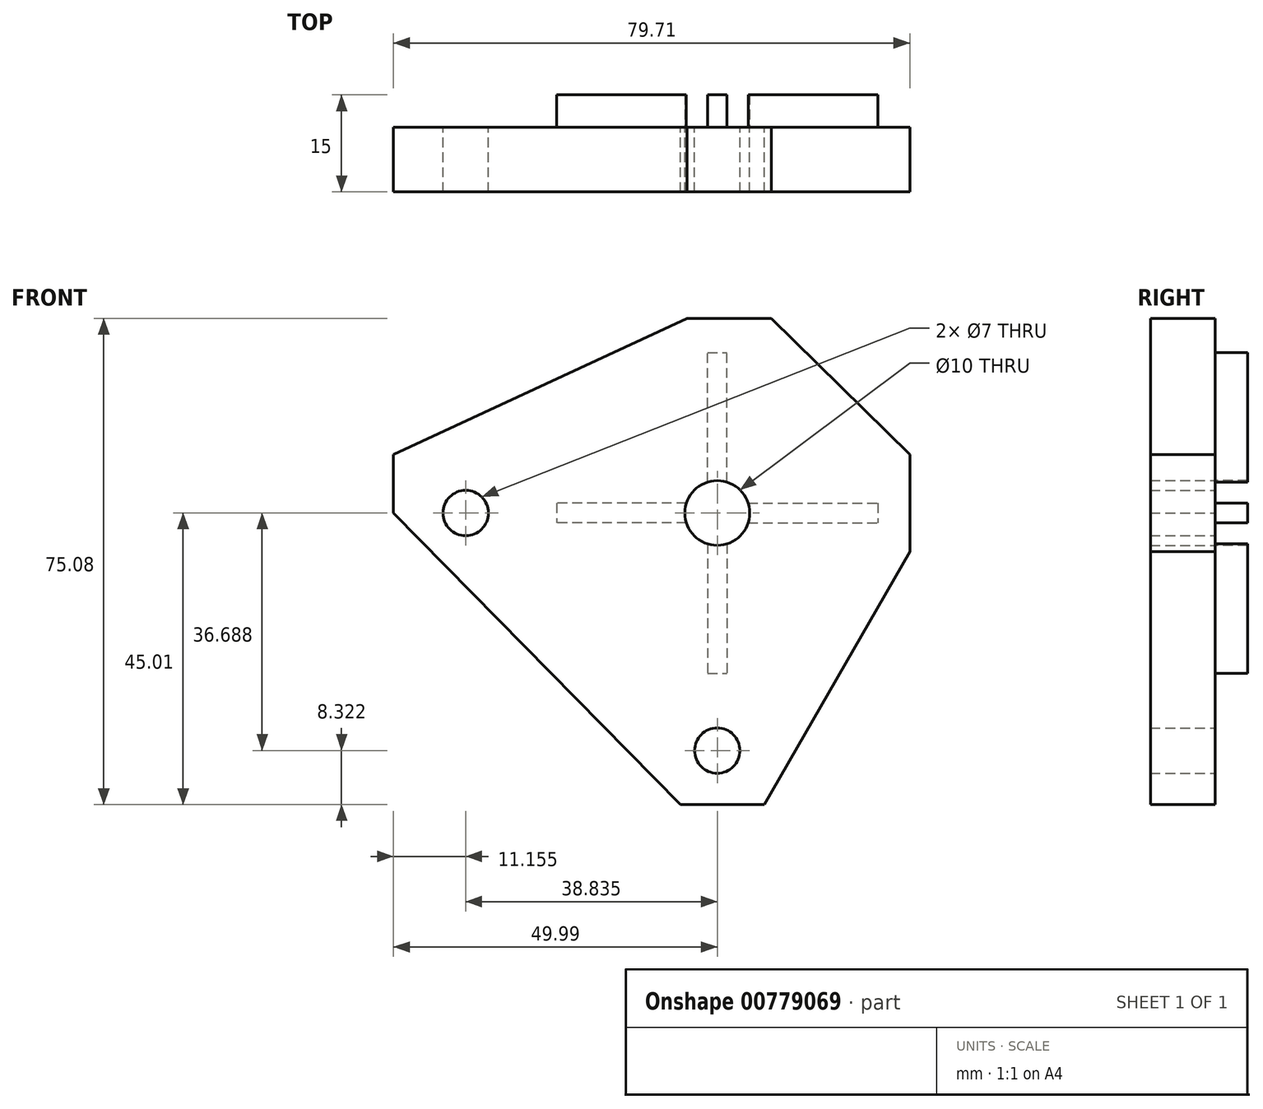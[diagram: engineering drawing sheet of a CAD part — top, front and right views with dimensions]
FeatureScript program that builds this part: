
annotation { "Feature Type Name" : "Feature", "Feature Type Description" : "" }
export const myFeature = defineFeature(function(context is Context, id is Id, definition is map)
    precondition{}
    {
        {
            var Q0;
            Q0=qCreatedBy(makeId("Front.planeOp"),FACE);
            var sketch = newSketch(context, id + "F0", { "sketchPlane" : qUnion([Q0])});
            skCircle(sketch, "E0", {"center": v(0, 0) * mm, "radius": 5 * mm});
            skLineSegment(sketch, "E1", {"start": v(0, 30.64) * mm, "end": v(0, -43.55) * mm, "construction": true});
            skLineSegment(sketch, "E2", {"start": v(-1.5, 4.77) * mm, "end": v(-1.5, 24.77) * mm});
            skLineSegment(sketch, "E3.MirrorCS", {"start": v(1.5, 4.77) * mm, "end": v(1.5, 24.77) * mm});
            skLineSegment(sketch, "E4", {"start": v(-1.5, 24.77) * mm, "end": v(1.5, 24.77) * mm});
            skLineSegment(sketch, "E5", {"start": v(-38.83, 0) * mm, "end": v(36.67, 0) * mm, "construction": true});
            skLineSegment(sketch, "E6.MirrorCS", {"start": v(1.5, -4.77) * mm, "end": v(1.5, -24.77) * mm});
            skLineSegment(sketch, "E7.MirrorCS", {"start": v(-1.5, -4.77) * mm, "end": v(-1.5, -24.77) * mm});
            skLineSegment(sketch, "E8.MirrorCS", {"start": v(-1.5, -24.77) * mm, "end": v(1.5, -24.77) * mm});
            skLineSegment(sketch, "E9", {"start": v(4.77, 1.5) * mm, "end": v(24.77, 1.5) * mm});
            skLineSegment(sketch, "E10.MirrorCS", {"start": v(4.77, -1.5) * mm, "end": v(24.77, -1.5) * mm});
            skLineSegment(sketch, "E11", {"start": v(24.77, 1.5) * mm, "end": v(24.77, -1.5) * mm});
            skLineSegment(sketch, "E12.MirrorCS", {"start": v(-4.77, 1.5) * mm, "end": v(-24.77, 1.5) * mm});
            skLineSegment(sketch, "E13.MirrorCS", {"start": v(-4.77, -1.5) * mm, "end": v(-24.77, -1.5) * mm});
            skLineSegment(sketch, "E14.MirrorCS", {"start": v(-24.77, 1.5) * mm, "end": v(-24.77, -1.5) * mm});
            skCircle(sketch, "E15", {"center": v(-38.83, 0) * mm, "radius": 3.5 * mm});
            skCircle(sketch, "E16", {"center": v(0, -36.69) * mm, "radius": 3.5 * mm});
            skLineSegment(sketch, "E17", {"start": v(-49.99, 0) * mm, "end": v(-5.7, -45.01) * mm});
            skLineSegment(sketch, "E18", {"start": v(-5.7, -45.01) * mm, "end": v(7.3, -45.01) * mm});
            skLineSegment(sketch, "E19", {"start": v(7.3, -45.01) * mm, "end": v(29.72, -6) * mm});
            skLineSegment(sketch, "E20", {"start": v(29.72, 2.8) * mm, "end": v(29.72, 9) * mm});
            skLineSegment(sketch, "E21", {"start": v(29.72, 9) * mm, "end": v(8.36, 30.07) * mm});
            skLineSegment(sketch, "E22", {"start": v(8.36, 30.07) * mm, "end": v(-4.64, 30.07) * mm});
            skLineSegment(sketch, "E23", {"start": v(-4.64, 30.07) * mm, "end": v(-49.99, 9) * mm});
            skLineSegment(sketch, "E24", {"start": v(-49.99, 9) * mm, "end": v(-49.99, 0) * mm});
            skLineSegment(sketch, "E25", {"start": v(29.72, 2.8) * mm, "end": v(29.72, -6) * mm});
            skSolve(sketch);
        }
        {
            var Q0;
            {var subQ0=sQuery(id+"F0.wireOp",EDGE,"E12.MirrorCS");Q0=makeQuery(id+"F0.imprint","IMPRINT",FACE,{"disambiguationData":[TD([[makeQuery(id+"F0.imprint","IMPRINT",EDGE,{"derivedFrom":subQ0}),1.0]])]});}
            var Q1;
            {var subQ0=sQuery(id+"F0.wireOp",EDGE,"E2");Q1=makeQuery(id+"F0.imprint","IMPRINT",FACE,{"disambiguationData":[TD([[makeQuery(id+"F0.imprint","IMPRINT",EDGE,{"derivedFrom":subQ0}),-1.0]])]});}
            var Q2;
            {var subQ0=sQuery(id+"F0.wireOp",EDGE,"E9");Q2=makeQuery(id+"F0.imprint","IMPRINT",FACE,{"disambiguationData":[TD([[makeQuery(id+"F0.imprint","IMPRINT",EDGE,{"derivedFrom":subQ0}),-1.0]])]});}
            var Q3;
            {var subQ0=sQuery(id+"F0.wireOp",EDGE,"E6.MirrorCS");Q3=makeQuery(id+"F0.imprint","IMPRINT",FACE,{"disambiguationData":[TD([[makeQuery(id+"F0.imprint","IMPRINT",EDGE,{"derivedFrom":subQ0}),-1.0]])]});}
            extrude(context, id + "F1", {"entities" : qUnion([Q0, Q1, Q2, Q3]), "depth" : -5 * mm, "offsetDistance" : 25 * mm});
        }
        {
            var Q0;
            {var subQ7=sQuery(id+"F0.wireOp",EDGE,"E2");Q0=makeQuery(id+"F0.imprint","IMPRINT",FACE,{"disambiguationData":[TD([[makeQuery(id+"F0.imprint","IMPRINT",EDGE,{"derivedFrom":subQ7}),1.0]])]});}
            var Q1;
            {var subQ0=sQuery(id+"F0.wireOp",EDGE,"E12.MirrorCS");Q1=makeQuery(id+"F0.imprint","IMPRINT",FACE,{"disambiguationData":[TD([[makeQuery(id+"F0.imprint","IMPRINT",EDGE,{"derivedFrom":subQ0}),1.0]])]});}
            var Q2;
            {var subQ0=sQuery(id+"F0.wireOp",EDGE,"E2");Q2=makeQuery(id+"F0.imprint","IMPRINT",FACE,{"disambiguationData":[TD([[makeQuery(id+"F0.imprint","IMPRINT",EDGE,{"derivedFrom":subQ0}),-1.0]])]});}
            var Q3;
            {var subQ0=sQuery(id+"F0.wireOp",EDGE,"E9");Q3=makeQuery(id+"F0.imprint","IMPRINT",FACE,{"disambiguationData":[TD([[makeQuery(id+"F0.imprint","IMPRINT",EDGE,{"derivedFrom":subQ0}),-1.0]])]});}
            var Q4;
            {var subQ0=sQuery(id+"F0.wireOp",EDGE,"E6.MirrorCS");Q4=makeQuery(id+"F0.imprint","IMPRINT",FACE,{"disambiguationData":[TD([[makeQuery(id+"F0.imprint","IMPRINT",EDGE,{"derivedFrom":subQ0}),-1.0]])]});}
            extrude(context, id + "F2", {"entities" : qUnion([Q0, Q1, Q2, Q3, Q4]), "depth" : 10 * mm, "offsetDistance" : 25 * mm});
        }
    });
